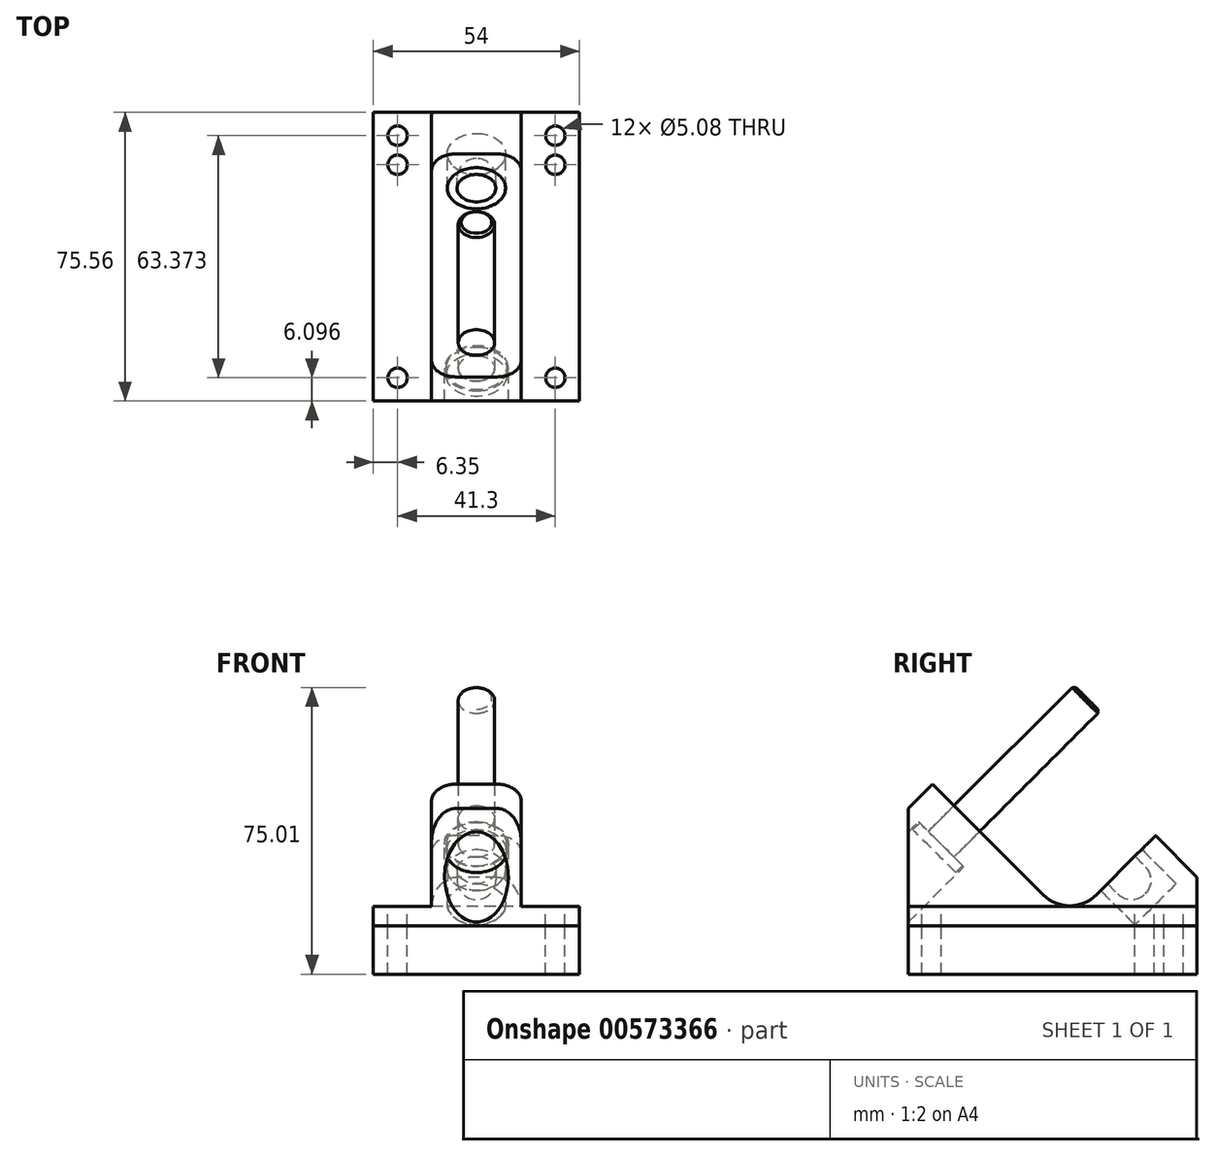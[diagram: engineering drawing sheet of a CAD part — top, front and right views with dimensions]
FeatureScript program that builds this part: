
annotation { "Feature Type Name" : "Feature", "Feature Type Description" : "" }
export const myFeature = defineFeature(function(context is Context, id is Id, definition is map)
    precondition{}
    {
        {
            var Q0;
            Q0=qCreatedBy(makeId("Right.planeOp"),FACE);
            var sketch = newSketch(context, id + "F0", { "sketchPlane" : qUnion([Q0])});
            skLineSegment(sketch, "E0", {"start": v(0, 0) * mm, "end": v(0, 30.7) * mm});
            skLineSegment(sketch, "E1", {"start": v(0, 30.7) * mm, "end": v(6.33, 37.03) * mm});
            skLineSegment(sketch, "E2", {"start": v(6.33, 37.03) * mm, "end": v(42.25, 1.1) * mm});
            skLineSegment(sketch, "E3", {"start": v(42.25, 1.1) * mm, "end": v(64.7, 23.56) * mm});
            skLineSegment(sketch, "E4", {"start": v(64.7, 23.56) * mm, "end": v(75.56, 12.7) * mm});
            skLineSegment(sketch, "E5", {"start": v(75.57, 12.7) * mm, "end": v(75.57, 0) * mm});
            skLineSegment(sketch, "E6", {"start": v(75.57, 0) * mm, "end": v(0, 0) * mm});
            skLineSegment(sketch, "E7", {"start": v(15.31, 28.05) * mm, "end": v(28.78, 41.52) * mm, "construction": true});
            skLineSegment(sketch, "E8", {"start": v(28.78, 41.52) * mm, "end": v(55.72, 14.58) * mm, "construction": true});
            skLineSegment(sketch, "E9", {"start": v(55.72, 14.58) * mm, "end": v(64.7, 5.6) * mm, "construction": true});
            skLineSegment(sketch, "E10", {"start": v(59.32, 0.21) * mm, "end": v(64.7, 5.6) * mm, "construction": true});
            skLineSegment(sketch, "E11", {"start": v(59.32, 0.21) * mm, "end": v(50.34, 9.2) * mm, "construction": true});
            skLineSegment(sketch, "E12", {"start": v(28.78, 41.52) * mm, "end": v(15.31, 55) * mm, "construction": true});
            skCircle(sketch, "E13", {"center": v(15.31, 55) * mm, "radius": 4 * mm, "construction": true});
            skLineSegment(sketch, "E14", {"start": v(61.11, 19.97) * mm, "end": v(70.1, 10.99) * mm, "construction": true});
            skLineSegment(sketch, "E15", {"start": v(70.1, 10.99) * mm, "end": v(64.7, 5.6) * mm, "construction": true});
            skCircle(sketch, "E16", {"center": v(58.42, 11.89) * mm, "radius": 5.08 * mm, "construction": true});
            skSolve(sketch);
        }
        {
            var Q0;
            Q0=makeQuery(id+"F0.imprint","IMPRINT",FACE,{"disambiguationData":[TD([[makeQuery(id+"F0.imprint","IMPRINT",EDGE,{"derivedFrom":sQuery(id+"F0.wireOp",EDGE,"E0")}),-1.0]])]});
            var Q1;
            Q1=makeQuery(id+"F0.imprint","IMPRINT",FACE,{"disambiguationData":[TD([[makeQuery(id+"F0.imprint","IMPRINT",EDGE,{"derivedFrom":sQuery(id+"F0.wireOp",EDGE,"E13")}),1.0]])]});
            extrude(context, id + "F1", {"entities" : qUnion([Q0, Q1]), "depth" : 27 * mm, "offsetDistance" : 25.4 * mm});
        }
        {
            var Q0;
            Q0=makeQuery(id+"F1.opExtrude","SWEPT_EDGE",EDGE,{"disambiguationData":[OSD([sQuery(id+"F0.wireOp",EDGE,"E2"),sQuery(id+"F0.wireOp",EDGE,"E3")])]});
            fillet(context, id + "F2", {"entities" : qUnion([Q0]), "radius" : 9.9 * mm, "tangentPropagation" : true, "allowEdgeOverflow" : false});
        }
        {
            var Q0;
            Q0=makeQuery(id+"F1.opExtrude","CAP_FACE",FACE,{"disambiguationData":[OSD([sQuery(id+"F0.wireOp",EDGE,"E0"),sQuery(id+"F0.wireOp",EDGE,"E1"),sQuery(id+"F0.wireOp",EDGE,"E2"),sQuery(id+"F0.wireOp",EDGE,"E3"),sQuery(id+"F0.wireOp",EDGE,"E4"),sQuery(id+"F0.wireOp",EDGE,"E5"),sQuery(id+"F0.wireOp",EDGE,"E6")])],"isStart":false});
            var sketch = newSketch(context, id + "F3", { "sketchPlane" : qUnion([Q0])});
            skLineSegment(sketch, "E17.bottom", {"start": v(0, 5.08) * mm, "end": v(75.57, 5.08) * mm});
            skLineSegment(sketch, "E17.top", {"start": v(0, 37.03) * mm, "end": v(75.57, 37.03) * mm});
            skLineSegment(sketch, "E17.left", {"start": v(0, 5.08) * mm, "end": v(0, 37.03) * mm});
            skLineSegment(sketch, "E17.right", {"start": v(75.57, 5.08) * mm, "end": v(75.57, 37.03) * mm});
            skSolve(sketch);
        }
        {
            var Q0;
            Q0 = qSketchRegion(id + "F3", true);
            extrude(context, id + "F4", {"entities" : qUnion([Q0]), "operationType" : NewBodyOperationType.REMOVE, "oppositeDirection" : true, "depth" : 15.24 * mm, "offsetDistance" : 25.4 * mm});
        }
        {
            var Q0;
            Q0=makeQuery(id+"F4.boolean.opBoolean","COPY",FACE,{"derivedFrom":makeQuery(id+"F4.opExtrude","SWEPT_FACE",FACE,{"disambiguationData":[OSD([sQuery(id+"F3.wireOp",EDGE,"E17.bottom")])]})});
            var sketch = newSketch(context, id + "F5", { "sketchPlane" : qUnion([Q0])});
            skLineSegment(sketch, "E18", {"start": v(20.65, 69.47) * mm, "end": v(20.65, 61.85) * mm, "construction": true});
            skLineSegment(sketch, "E19", {"start": v(20.65, 61.85) * mm, "end": v(20.65, 6.1) * mm, "construction": true});
            skCircle(sketch, "E20", {"center": v(20.65, 69.47) * mm, "radius": 2.54 * mm});
            skCircle(sketch, "E21", {"center": v(20.65, 61.85) * mm, "radius": 2.54 * mm});
            skCircle(sketch, "E22", {"center": v(20.65, 6.1) * mm, "radius": 2.54 * mm});
            skSolve(sketch);
        }
        {
            var Q0;
            Q0 = qSketchRegion(id + "F5", true);
            extrude(context, id + "F6", {"entities" : qUnion([Q0]), "operationType" : NewBodyOperationType.REMOVE, "endBound" : BoundingType.THROUGH_ALL, "oppositeDirection" : true, "depth" : 25.4 * mm, "offsetDistance" : 25.4 * mm});
        }
        {
            var Q0;
            Q0=makeQuery(id+"F1.opExtrude","SWEPT_BODY",BODY,{"disambiguationData":[OSD([sQuery(id+"F0.wireOp",EDGE,"E0"),sQuery(id+"F0.wireOp",EDGE,"E1"),sQuery(id+"F0.wireOp",EDGE,"E2"),sQuery(id+"F0.wireOp",EDGE,"E3"),sQuery(id+"F0.wireOp",EDGE,"E4"),sQuery(id+"F0.wireOp",EDGE,"E5"),sQuery(id+"F0.wireOp",EDGE,"E6")])]});
            var Q1;
            Q1=makeQuery(id+"F1.opExtrude","CAP_FACE",FACE,{"disambiguationData":[OSD([sQuery(id+"F0.wireOp",EDGE,"E0"),sQuery(id+"F0.wireOp",EDGE,"E1"),sQuery(id+"F0.wireOp",EDGE,"E2"),sQuery(id+"F0.wireOp",EDGE,"E3"),sQuery(id+"F0.wireOp",EDGE,"E4"),sQuery(id+"F0.wireOp",EDGE,"E5"),sQuery(id+"F0.wireOp",EDGE,"E6")])],"isStart":true});
            mirror(context, id + "F7", {"operationType" : NewBodyOperationType.ADD, "entities" : qUnion([Q0]), "mirrorPlane" : qUnion([Q1])});
        }
        {
            var Q0;
            Q0=makeQuery(id+"F7.opPattern","COPY",EDGE,{"derivedFrom":makeQuery(id+"F4.boolean.opBoolean","INTERSECT",EDGE,{"derivedFrom":[makeQuery(id+"F1.opExtrude","SWEPT_FACE",FACE,{"disambiguationData":[OSD([sQuery(id+"F0.wireOp",EDGE,"E4")])]}),makeQuery(id+"F4.opExtrude","CAP_FACE",FACE,{"disambiguationData":[OSD([sQuery(id+"F3.wireOp",EDGE,"E17.bottom"),sQuery(id+"F3.wireOp",EDGE,"E17.top"),sQuery(id+"F3.wireOp",EDGE,"E17.left"),sQuery(id+"F3.wireOp",EDGE,"E17.right")])],"isStart":false})]}),"instanceName":"1"});
            var Q1;
            Q1=makeQuery(id+"F7.opPattern","COPY",EDGE,{"derivedFrom":makeQuery(id+"F4.boolean.opBoolean","INTERSECT",EDGE,{"derivedFrom":[makeQuery(id+"F1.opExtrude","SWEPT_FACE",FACE,{"disambiguationData":[OSD([sQuery(id+"F0.wireOp",EDGE,"E1")])]}),makeQuery(id+"F4.opExtrude","CAP_FACE",FACE,{"disambiguationData":[OSD([sQuery(id+"F3.wireOp",EDGE,"E17.bottom"),sQuery(id+"F3.wireOp",EDGE,"E17.top"),sQuery(id+"F3.wireOp",EDGE,"E17.left"),sQuery(id+"F3.wireOp",EDGE,"E17.right")])],"isStart":false})]}),"instanceName":"1"});
            var Q2;
            Q2=makeQuery(id+"F4.boolean.opBoolean","INTERSECT",EDGE,{"derivedFrom":[makeQuery(id+"F1.opExtrude","SWEPT_FACE",FACE,{"disambiguationData":[OSD([sQuery(id+"F0.wireOp",EDGE,"E1")])]}),makeQuery(id+"F4.opExtrude","CAP_FACE",FACE,{"disambiguationData":[OSD([sQuery(id+"F3.wireOp",EDGE,"E17.bottom"),sQuery(id+"F3.wireOp",EDGE,"E17.top"),sQuery(id+"F3.wireOp",EDGE,"E17.left"),sQuery(id+"F3.wireOp",EDGE,"E17.right")])],"isStart":false})]});
            var Q3;
            Q3=makeQuery(id+"F4.boolean.opBoolean","INTERSECT",EDGE,{"derivedFrom":[makeQuery(id+"F1.opExtrude","SWEPT_FACE",FACE,{"disambiguationData":[OSD([sQuery(id+"F0.wireOp",EDGE,"E4")])]}),makeQuery(id+"F4.opExtrude","CAP_FACE",FACE,{"disambiguationData":[OSD([sQuery(id+"F3.wireOp",EDGE,"E17.bottom"),sQuery(id+"F3.wireOp",EDGE,"E17.top"),sQuery(id+"F3.wireOp",EDGE,"E17.left"),sQuery(id+"F3.wireOp",EDGE,"E17.right")])],"isStart":false})]});
            fillet(context, id + "F8", {"entities" : qUnion([Q0, Q1, Q2, Q3]), "radius" : 6.35 * mm, "tangentPropagation" : true, "allowEdgeOverflow" : false});
        }
        {
            var Q0;
            Q0=qCreatedBy(makeId("Right.planeOp"),FACE);
            var sketch = newSketch(context, id + "F9", { "sketchPlane" : qUnion([Q0])});
            skLineSegment(sketch, "E23.0", {"start": v(15.31, 28.05) * mm, "end": v(28.78, 41.52) * mm, "construction": true});
            skLineSegment(sketch, "E23.1", {"start": v(6.33, 37.03) * mm, "end": v(42.25, 1.1) * mm, "construction": true});
            skLineSegment(sketch, "E24", {"start": v(15.31, 28.05) * mm, "end": v(11.95, 31.42) * mm});
            skLineSegment(sketch, "E25", {"start": v(11.95, 31.42) * mm, "end": v(5.21, 24.68) * mm});
            skLineSegment(sketch, "E26", {"start": v(5.21, 24.68) * mm, "end": v(2.68, 27.22) * mm});
            skLineSegment(sketch, "E27", {"start": v(2.68, 27.22) * mm, "end": v(-12.27, 12.27) * mm});
            skLineSegment(sketch, "E28", {"start": v(-12.27, 12.27) * mm, "end": v(-6.37, 6.37) * mm});
            skLineSegment(sketch, "E29", {"start": v(-6.37, 6.37) * mm, "end": v(15.31, 28.05) * mm});
            skLineSegment(sketch, "E30", {"start": v(-6.37, 6.37) * mm, "end": v(0, 0) * mm, "construction": true});
            skSolve(sketch);
        }
        {
            var Q0;
            Q0 = qSketchRegion(id + "F9", true);
            var Q1;
            Q1=sQuery(id+"F9.wireOp",EDGE,"E23.0");
            revolve(context, id + "F10", {"operationType" : NewBodyOperationType.REMOVE, "entities" : qUnion([Q0]), "axis" : qUnion([Q1]), "revolveType" : RevolveType.FULL, "oppositeDirection" : true});
        }
        {
            var Q0;
            Q0=qCreatedBy(makeId("Right.planeOp"),FACE);
            var sketch = newSketch(context, id + "F11", { "sketchPlane" : qUnion([Q0])});
            skLineSegment(sketch, "E31.1", {"start": v(5.21, 24.68) * mm, "end": v(2.97, 26.93) * mm});
            skLineSegment(sketch, "E31.2", {"start": v(11.95, 31.42) * mm, "end": v(5.21, 24.68) * mm});
            skLineSegment(sketch, "E32", {"start": v(2.97, 26.93) * mm, "end": v(1.17, 25.13) * mm});
            skPoint(sketch, "E31.0.end.orphan", {"position": v(-12.27, 12.27) * mm});
            skPoint(sketch, "E31.0.start.orphan", {"position": v(2.68, 27.22) * mm});
            skLineSegment(sketch, "E33", {"start": v(1.17, 25.13) * mm, "end": v(6.78, 19.52) * mm});
            skLineSegment(sketch, "E34", {"start": v(6.78, 19.52) * mm, "end": v(46.74, 59.48) * mm});
            skLineSegment(sketch, "E35", {"start": v(46.74, 59.48) * mm, "end": v(43.38, 62.85) * mm});
            skLineSegment(sketch, "E36", {"start": v(43.38, 62.85) * mm, "end": v(11.95, 31.42) * mm});
            skSolve(sketch);
        }
        {
            var Q0;
            Q0 = qSketchRegion(id + "F11", true);
            var Q1;
            Q1=sQuery(id+"F11.wireOp",EDGE,"E34");
            revolve(context, id + "F12", {"entities" : qUnion([Q0]), "axis" : qUnion([Q1]), "revolveType" : RevolveType.FULL});
        }
        {
            var Q0;
            Q0=makeQuery(id+"F12.opRevolve","SWEPT_EDGE",EDGE,{"disambiguationData":[OSD([sQuery(id+"F11.wireOp",EDGE,"E35"),sQuery(id+"F11.wireOp",EDGE,"E36")])]});
            chamfer(context, id + "F13", {"entities" : qUnion([Q0]), "width" : 0.76 * mm, "tangentPropagation" : true});
        }
        {
            var Q0;
            Q0=qCreatedBy(makeId("Right.planeOp"),FACE);
            var sketch = newSketch(context, id + "F14", { "sketchPlane" : qUnion([Q0])});
            skLineSegment(sketch, "E37", {"start": v(55.72, 14.58) * mm, "end": v(61.11, 19.97) * mm});
            skLineSegment(sketch, "E38", {"start": v(61.11, 19.97) * mm, "end": v(70.1, 10.99) * mm});
            skLineSegment(sketch, "E39", {"start": v(70.1, 10.99) * mm, "end": v(64.7, 5.6) * mm});
            skLineSegment(sketch, "E40", {"start": v(64.7, 5.6) * mm, "end": v(55.72, 14.58) * mm});
            skSolve(sketch);
        }
        {
            var Q0;
            Q0 = qSketchRegion(id + "F14", true);
            var Q1;
            Q1=sQuery(id+"F14.wireOp",EDGE,"E40");
            revolve(context, id + "F15", {"operationType" : NewBodyOperationType.REMOVE, "entities" : qUnion([Q0]), "axis" : qUnion([Q1]), "revolveType" : RevolveType.FULL, "oppositeDirection" : true});
        }
        {
            var Q0;
            {var subQ0=makeQuery(id+"F1.opExtrude","SWEPT_FACE",FACE,{"disambiguationData":[OSD([sQuery(id+"F0.wireOp",EDGE,"E6")])]});Q0=makeQuery(id+"F7.boolean.opBoolean","MERGE",FACE,{"derivedFrom":[subQ0,makeQuery(id+"F7.opPattern","COPY",FACE,{"derivedFrom":subQ0,"instanceName":"1"})]});}
            extrude(context, id + "F16", {"entities" : qUnion([Q0]), "depth" : 12.7 * mm, "offsetDistance" : 25.4 * mm});
        }
        {
            var Q0;
            Q0=qCreatedBy(makeId("Right.planeOp"),FACE);
            var sketch = newSketch(context, id + "F17", { "sketchPlane" : qUnion([Q0])});
            skArc(sketch, "E41", {"start": v(62.01, 15.48) * mm, "mid": v(63.5, 11.89) * mm, "end": v(62.01, 8.3) * mm});
            skLineSegment(sketch, "E42", {"start": v(62.01, 15.48) * mm, "end": v(59.32, 18.17) * mm});
            skLineSegment(sketch, "E43", {"start": v(59.32, 18.17) * mm, "end": v(61.11, 19.97) * mm});
            skLineSegment(sketch, "E44", {"start": v(61.11, 19.97) * mm, "end": v(70.1, 10.99) * mm});
            skLineSegment(sketch, "E45", {"start": v(70.1, 10.99) * mm, "end": v(64.7, 5.6) * mm});
            skLineSegment(sketch, "E46", {"start": v(64.7, 5.6) * mm, "end": v(62.01, 8.3) * mm});
            skLineSegment(sketch, "E47", {"start": v(58.42, 11.89) * mm, "end": v(62.01, 15.48) * mm, "construction": true});
            skLineSegment(sketch, "E48", {"start": v(62.01, 8.3) * mm, "end": v(58.42, 11.89) * mm, "construction": true});
            skSolve(sketch);
        }
        {
            var Q0;
            Q0 = qSketchRegion(id + "F17", true);
            var Q1;
            Q1=sQuery(id+"F17.wireOp",EDGE,"E48");
            revolve(context, id + "F18", {"entities" : qUnion([Q0]), "axis" : qUnion([Q1]), "revolveType" : RevolveType.FULL});
        }
    });
